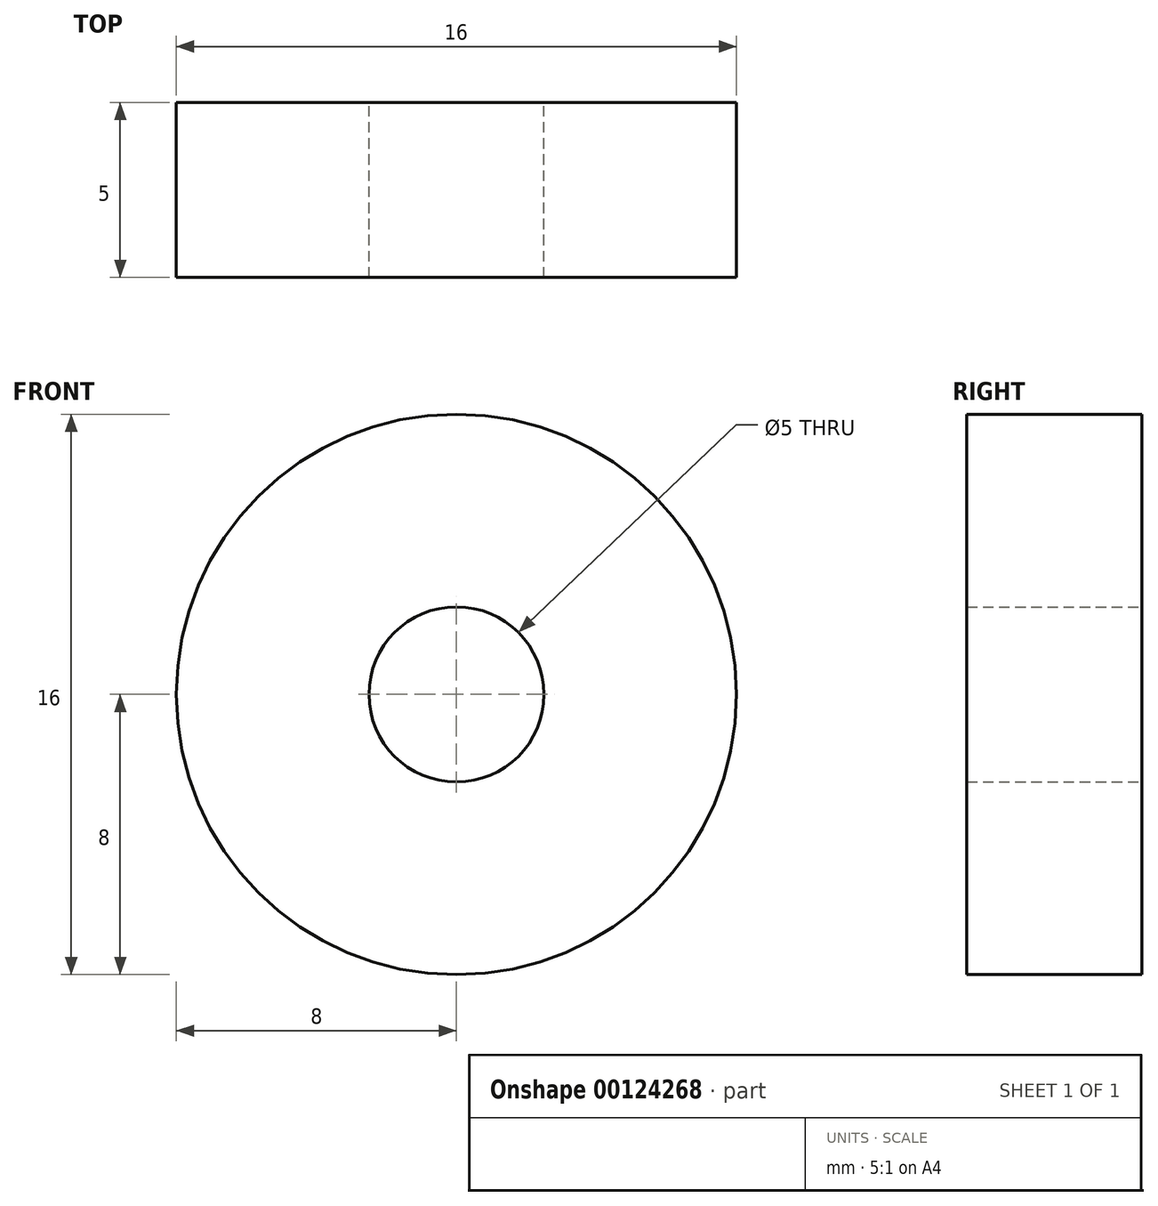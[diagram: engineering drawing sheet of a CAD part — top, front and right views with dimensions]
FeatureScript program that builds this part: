
annotation { "Feature Type Name" : "Feature", "Feature Type Description" : "" }
export const myFeature = defineFeature(function(context is Context, id is Id, definition is map)
    precondition{}
    {
        {
            var Q0;
            Q0=qCreatedBy(makeId("Front.planeOp"),FACE);
            var sketch = newSketch(context, id + "F0", { "sketchPlane" : qUnion([Q0])});
            skCircle(sketch, "E0", {"center": v(0, 0) * mm, "radius": 8 * mm});
            skCircle(sketch, "E1", {"center": v(0, 0) * mm, "radius": 2.5 * mm});
            skSolve(sketch);
        }
        {
            var Q0;
            Q0 = qSketchRegion(id + "F0", true);
            extrude(context, id + "F1", {"entities" : qUnion([Q0]), "depth" : 5 * mm});
        }
    });
